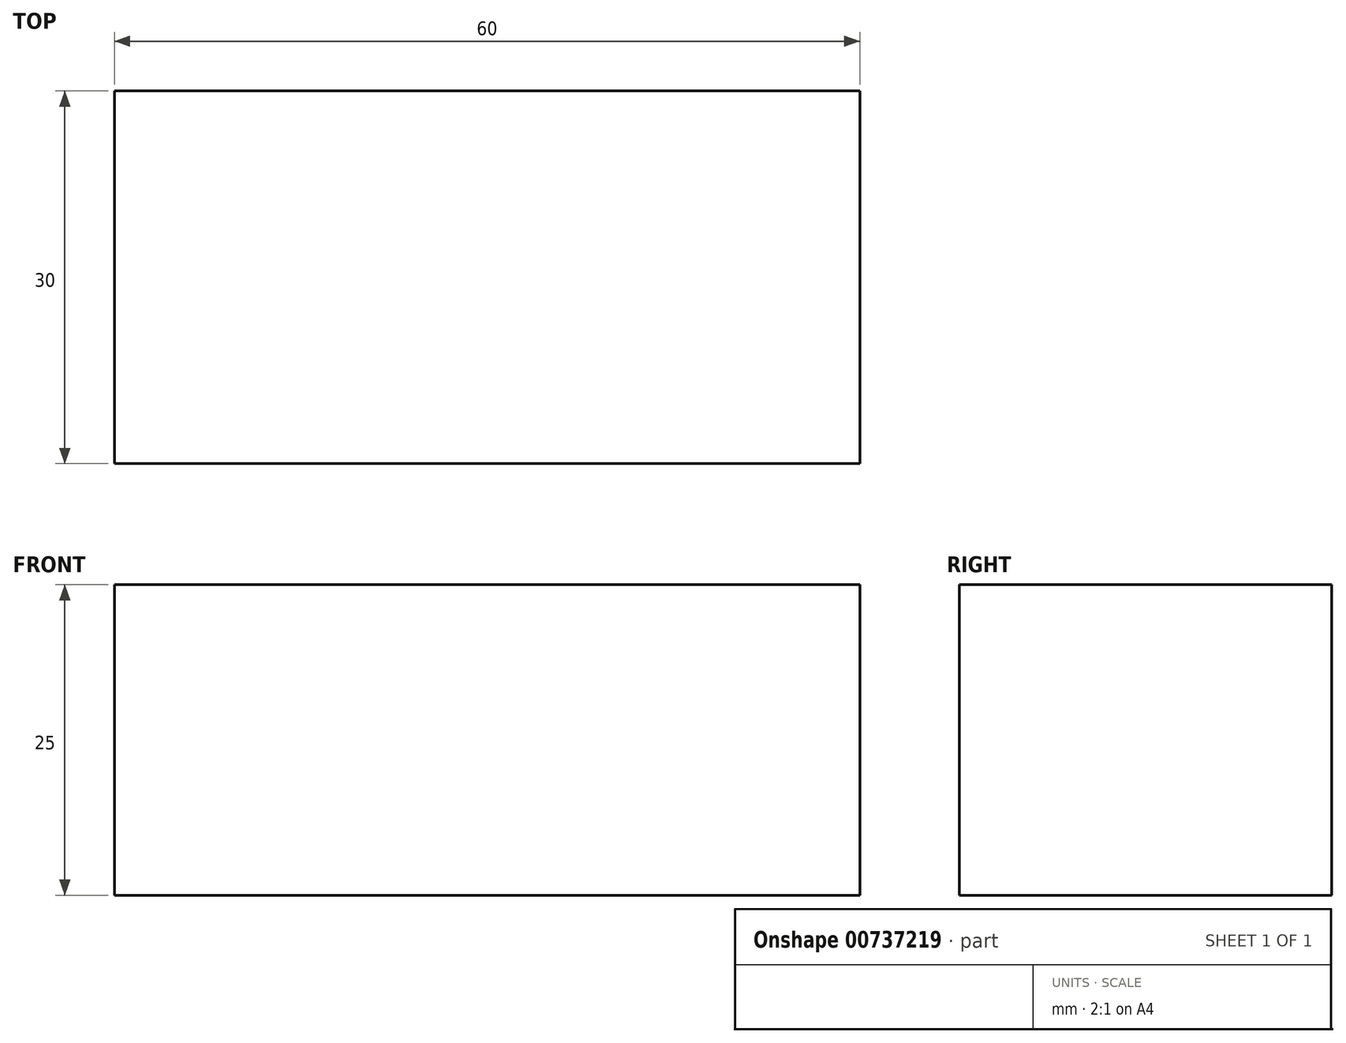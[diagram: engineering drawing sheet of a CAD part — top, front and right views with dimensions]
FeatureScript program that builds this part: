
annotation { "Feature Type Name" : "Feature", "Feature Type Description" : "" }
export const myFeature = defineFeature(function(context is Context, id is Id, definition is map)
    precondition{}
    {
        {
            var Q0;
            Q0=qCreatedBy(makeId("Top.planeOp"),FACE);
            var sketch = newSketch(context, id + "F0", { "sketchPlane" : qUnion([Q0])});
            skLineSegment(sketch, "E0.bottom", {"start": v(0, 0) * mm, "end": v(60, 0) * mm});
            skLineSegment(sketch, "E0.top", {"start": v(0, 30) * mm, "end": v(60, 30) * mm});
            skLineSegment(sketch, "E0.left", {"start": v(0, 0) * mm, "end": v(0, 30) * mm});
            skLineSegment(sketch, "E0.right", {"start": v(60, 0) * mm, "end": v(60, 30) * mm});
            skSolve(sketch);
        }
        {
            var Q0;
            Q0 = qSketchRegion(id + "F0", true);
            extrude(context, id + "F1", {"entities" : qUnion([Q0]), "depth" : 25 * mm, "offsetDistance" : 25 * mm});
        }
    });
